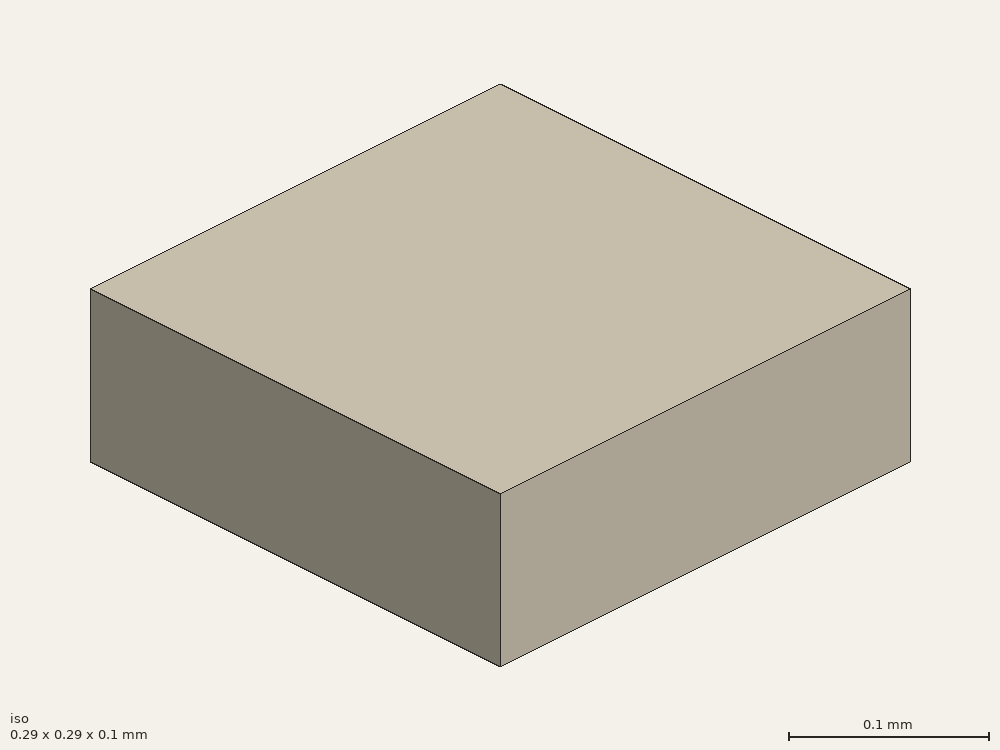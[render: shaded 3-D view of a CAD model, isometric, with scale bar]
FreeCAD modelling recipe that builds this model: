
FCSTD DOCUMENT  (FreeCAD 0.17R12607 (Git))
Label: 1616 RGB LED Blue
License: CreativeCommons Attribution-ShareAlike
LicenseURL: http://creativecommons.org/licenses/by-sa/4.0/
objects: Sketcher::SketchObject×1, PartDesign::Pad×1, PartDesign::Body×1
note: 4 computed .brp shape members not serialized (recipe doc carries the construction recipe); baked Part::Feature solids carry a one-line shape summary decoded from their .brp

FEATURE [Sketcher::SketchObject] Sketch
  MapMode = 5
  Support = -> [XY_Plane]
  sketch-geometry (4):
    g0: LineSegment StartX=-0.145 StartY=0.145 StartZ=0 EndX=0.145 EndY=0.145 EndZ=0
    g1: LineSegment StartX=0.145 StartY=0.145 StartZ=0 EndX=0.145 EndY=-0.145 EndZ=0
    g2: LineSegment StartX=0.145 StartY=-0.145 StartZ=0 EndX=-0.145 EndY=-0.145 EndZ=0
    g3: LineSegment StartX=-0.145 StartY=-0.145 StartZ=0 EndX=-0.145 EndY=0.145 EndZ=0
  constraints (12):
    c: Coincident(g0,g1)
    c: Coincident(g1,g2)
    c: Coincident(g2,g3)
    c: Coincident(g3,g0)
    c: Horizontal(g0)
    c: Horizontal(g2)
    c: Vertical(g1)
    c: Vertical(g3)
    c: Symmetric(g0,g0,g-2)
    c: Symmetric(g0,g1,g-1)
    c: Equal(g0,g1)
    c: DistanceY(g1,g1) = 0.29
FEATURE [PartDesign::Pad] Pad
  Length = 0.1
  Length2 = 100
  Profile = -> Sketch
  Type = 0
FEATURE [PartDesign::Body] Body
  Group = -> [Sketch,Pad]
  Origin = -> Origin
  Tip = -> Pad
